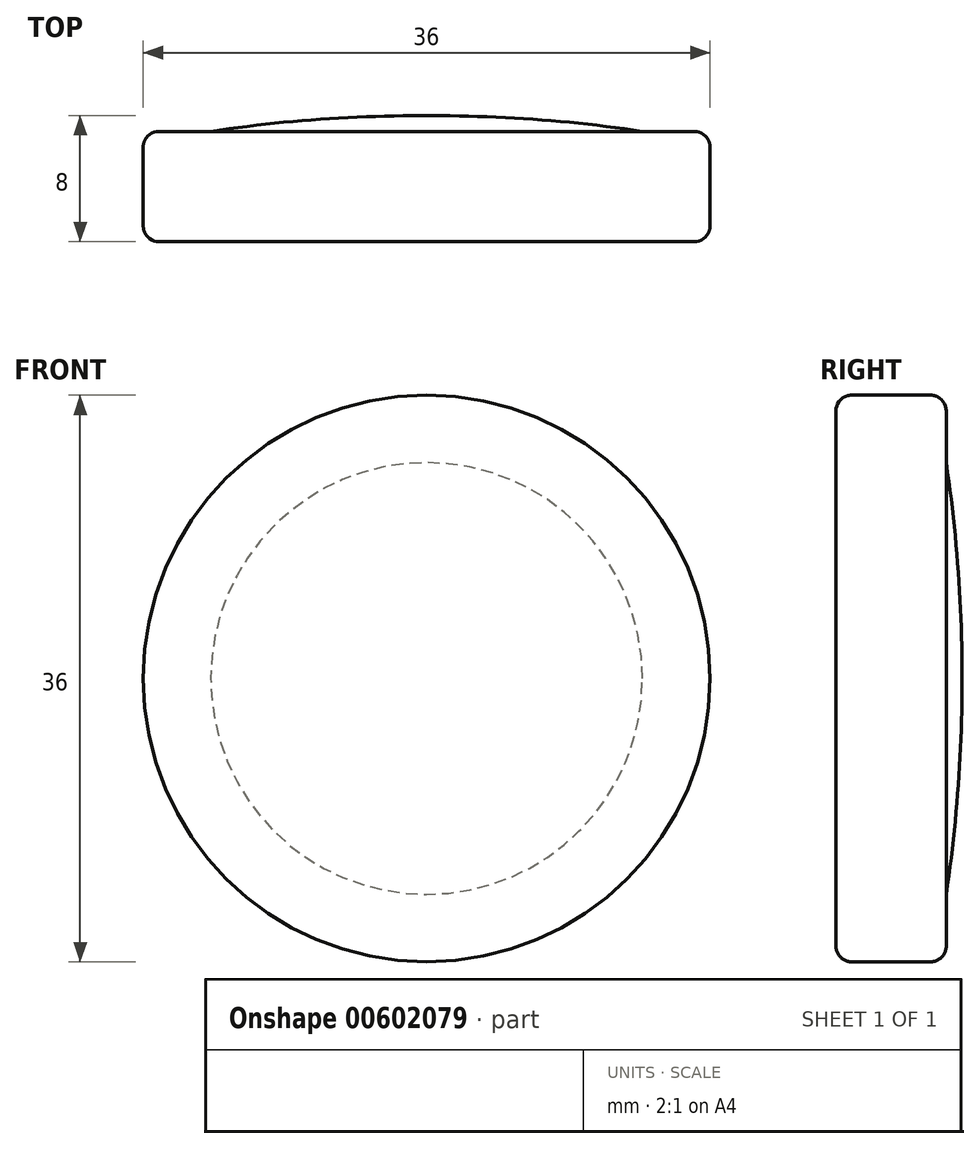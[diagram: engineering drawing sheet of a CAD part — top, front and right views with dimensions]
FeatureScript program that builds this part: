
annotation { "Feature Type Name" : "Feature", "Feature Type Description" : "" }
export const myFeature = defineFeature(function(context is Context, id is Id, definition is map)
    precondition{}
    {
        {
            var Q0;
            Q0=qCreatedBy(makeId("Front.planeOp"),FACE);
            var sketch = newSketch(context, id + "F0", { "sketchPlane" : qUnion([Q0])});
            skCircle(sketch, "E0", {"center": v(0, 0) * mm, "radius": 18 * mm});
            skCircle(sketch, "E1", {"center": v(0, 0) * mm, "radius": 13.67 * mm});
            skSolve(sketch);
        }
        {
            var Q0;
            Q0=qCreatedBy(makeId("Front.planeOp"),FACE);
            var sketch = newSketch(context, id + "F1", { "sketchPlane" : qUnion([Q0])});
            skCircle(sketch, "E2", {"center": v(0, 0) * mm, "radius": 13.7 * mm});
            skSolve(sketch);
        }
        {
            var Q0;
            Q0=makeQuery(id+"F0.imprint","IMPRINT",FACE,{"disambiguationData":[TD([[makeQuery(id+"F0.imprint","IMPRINT",EDGE,{"derivedFrom":sQuery(id+"F0.wireOp",EDGE,"E0")}),1.0]])]});
            extrude(context, id + "F2", {"entities" : qUnion([Q0]), "oppositeDirection" : true, "depth" : 7 * mm, "offsetDistance" : 25 * mm});
        }
        {
            var Q0;
            Q0=makeQuery(id+"F1.imprint","IMPRINT",FACE,{"disambiguationData":[TD([[makeQuery(id+"F1.imprint","IMPRINT",EDGE,{"derivedFrom":sQuery(id+"F1.wireOp",EDGE,"E2")}),1.0]])]});
            extrude(context, id + "F3", {"entities" : qUnion([Q0]), "operationType" : NewBodyOperationType.ADD, "oppositeDirection" : true, "depth" : 8 * mm, "offsetDistance" : 25 * mm});
        }
        {
            var Q0;
            Q0=makeQuery(id+"F2.opExtrude","SWEPT_FACE",FACE,{"disambiguationData":[OSD([sQuery(id+"F0.wireOp",EDGE,"E0")])]});
            fillet(context, id + "F4", {"entities" : qUnion([Q0]), "radius" : 1 * mm, "tangentPropagation" : true, "allowEdgeOverflow" : false});
        }
        {
            var Q0;
            Q0=makeQuery(id+"F3.opExtrude","CAP_FACE",FACE,{"disambiguationData":[OSD([sQuery(id+"F1.wireOp",EDGE,"E2")])],"isStart":false});
            fillet(context, id + "F5", {"entities" : qUnion([Q0]), "radius" : 90 * mm, "tangentPropagation" : true, "allowEdgeOverflow" : false});
        }
    });
